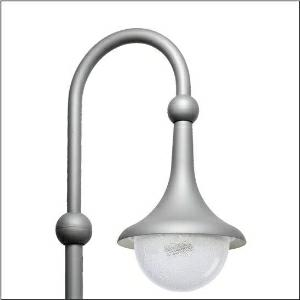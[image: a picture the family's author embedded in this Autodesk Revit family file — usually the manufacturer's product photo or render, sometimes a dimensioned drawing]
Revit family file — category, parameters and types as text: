
# Revit family: grosse_glocke___st1_2a_5xa1563e1b208_1d7c
name_source: partatom
category: Lighting Fixtures
units: mm (PartAtom-declared; Revit-internal decimal feet)

## family parameters
Cut with Voids When Loaded = No
Host = Face
Light Source = No
Part Type = Normal
Room Calculation Point = No
Round Connector Dimension = Use Diameter
Shared = No

## types (1)
- --- (1 x LED, 3210 lm, 23.4 W, 3000K)
    Apparent Load = 23 VA
    CIE Flux Codes = 29 66 94 99 100
    Color Rendering = 70
    Color Temperature = 3000K
    Default Elevation = 1800 mm
    Description = Large Bell, mast luminaire, primary light control with 3 zone facetted reflector, of plastic, silver coated, primary optical cover: enclosure, of PMMA, transparent structured, light distribution: ST1.2a, light emission: direct distribution, primary light characteristic: asymmetric, installation type: suspended mounting, LED, High Power LED, rated luminous flux: 3.210lm, luminous efficacy: 137lm/W, light colour: 730, colour temperature: 3000K, control gear: Plus, control: flexible luminous flux parameterisation, time-dependent luminous flux control, constant luminous flux control, digital communication interface, power reduction, electronic power reduction, mains connection: 230..240V, AC, 50/60Hz, start of lifetime: 23W, end of service life: 24W, reduction: 12W, luminaire housing, bell-shaped, of glass-fibre reinforced polyester, coated, Siteco® metallic grey (DB 702S), please order curved mast extension separately, diameter: 530mm, height: 695mm, mounting height: 4..6m, protection rating (complete): IP54, insulation class (complete): insulation class II (safety insulation), certification: CE, ENEC, VDE, impact resistance: IK08, standard-compliant lighting for roads and squares, packaging unit: 1 piece

Light Distribution: ST1.2a
    Height = 695 mm
    Lamp = 1 x LED
    Lamp Light Flux = 3210 lm
    Lamp Power = 23.4 W
    Lamp count = 1
    Length = 530 mm
    Luminous efficacy = 137 lm/W
    Manufacturer = Siteco
    ModVariant = No
    Model = 5XA1563E1B208
    Number of Poles = 1
    OnlyDefault = Yes
    Power Factor = 1
    Product Name = Große Glocke | ST1.2a
    Product group = mast luminaire | pylon annexe
    ProductGroupID = 6201
    Protection Class = Protection class II
    Protection Degree = IP 54
    RLX_Detail_Level = 1
    RLX_Emergency_Light_Flux = 0 lm
    RLX_Emergency_Type = 0
    RLX_Emergency_Type_DB = No
    RlxData = <blob elided: 54869 chars, md5=a10b93ee>
    Socket = socket
    Standby Power = 0 W
    System Light Flux = 3210 lm
    System Power = 23 W
    Type Comments = factory setting: luminous flux: 100 % | dim-lin: 254 | 460 mA
    Type Image = l_1347684.jpg
    URL = http://relux.com
    VarID = @adj_158950
    Voltage = 0 V
    Weight = 0.00 kg
    Width = 0 mm  [stored 0 ft]

note: [stored X ft] marks values corroborated as IEEE doubles in the binary element streams (Revit-internal decimal feet)

## geometry (parser evidence)
native form markers: Blend x4, Sweep x11
no freeform markers — native parametric forms only
